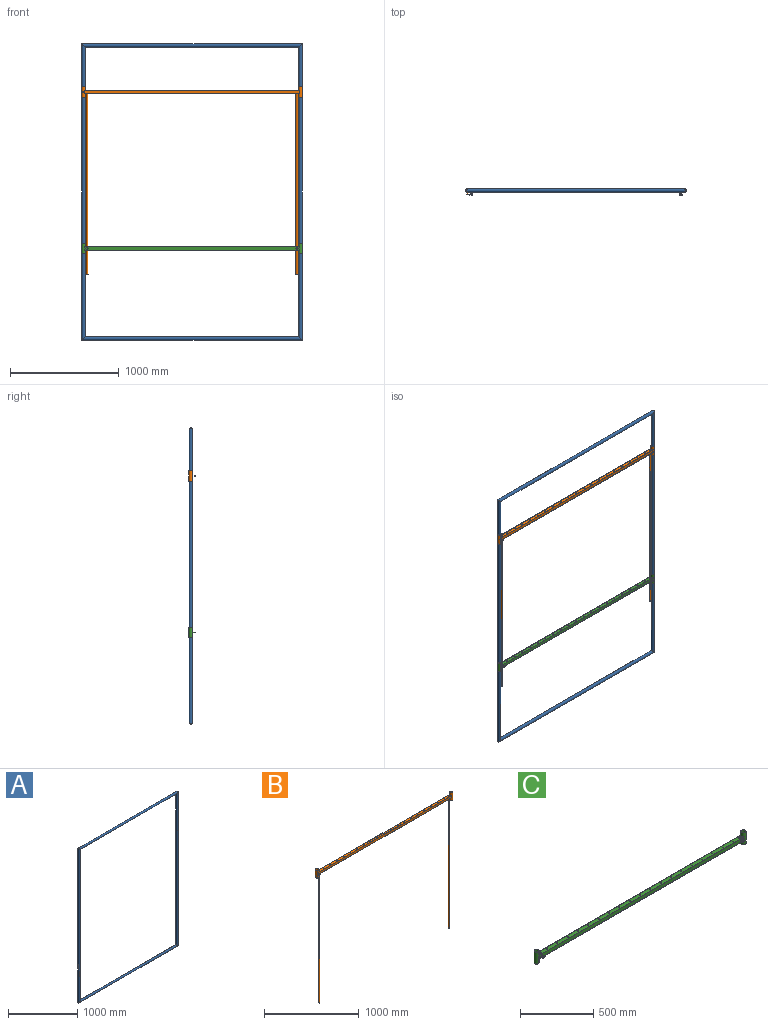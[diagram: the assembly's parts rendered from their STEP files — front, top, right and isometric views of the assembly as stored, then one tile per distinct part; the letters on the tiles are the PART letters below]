
ASSEMBLY  parts=3 mates=2
PART A: 8 faces, bbox 2030x30x2730 mm
  f0: cylinder r=15mm len=2030.02mm, axis (-1,0,0), area 188495.6mm2, adj f1,f3
  f1: cylinder r=15mm len=2730.02mm, axis (0,0,-1), area 254469mm2, adj f0,f2
  f2: cylinder r=15mm len=2030.02mm, axis (1,0,0), area 188495.6mm2, adj f1,f3
  f3: cylinder r=15mm len=2730.02mm, axis (0,0,1), area 254469mm2, adj f0,f2
  f4: cylinder r=13.5mm len=2027.01mm, axis (-1,0,0), area 169646mm2, adj f5,f7
  f5: cylinder r=13.5mm len=2727.01mm, axis (0,0,-1), area 229022.1mm2, adj f4,f6
  f6: cylinder r=13.5mm len=2027.01mm, axis (1,0,0), area 169646mm2, adj f5,f7
  f7: cylinder r=13.5mm len=2727.01mm, axis (0,0,1), area 229022.1mm2, adj f4,f6
PART B: 113 faces, bbox 2035x57.1x1735 mm
  f0: plane 5.12x1.44mm, normal (0,-1,0), area 5.2mm2, adj f96,f100
  f1: plane 9.2x0.1mm, normal (0,-1,0), area 0.9mm2, adj f2,f61,f67,f85
  f2: cylinder r=16mm len=100mm, axis (0,0,1), area 3788.6mm2, adj f1,f4,f49,f50,f59,f60,f61,f62
  f3: cylinder r=17.5mm len=100mm, axis (0,0,1), area 9735.8mm2, adj f49,f50,f51,f52,f53,f54,f87,f88
  f4: cylinder r=16mm len=100mm, axis (0,0,1), area 4969.3mm2, adj f2,f49,f50,f79,f80,f81,f82,f83
  f5: cylinder r=17.5mm len=27mm, axis (0,0,1), area 832.6mm2, adj f6,f7,f8,f9
  f6: plane 1977.73x27mm, normal (0,0,1), area 51802.5mm2, adj f5,f7,f9,f10,f30,f31,f32,f33
  f7: plane 1977.73x27mm, normal (0,-1,0), area 53398.7mm2, adj f5,f6,f8,f10
  f8: plane 1977.73x27mm, normal (0,0,-1), area 51802.5mm2, adj f5,f7,f9,f10,f11,f12,f13,f14
  f9: plane 1977.73x27mm, normal (0,1,0), area 53398.7mm2, adj f5,f6,f8,f10
  f10: cylinder r=17.5mm len=27mm, axis (0,0,1), area 832.6mm2, adj f6,f7,f8,f9
  f11: cylinder r=4mm len=8mm, axis (0,0,1), area 37.7mm2, adj f8,f52
  f12: cylinder r=4mm len=8mm, axis (0,0,1), area 37.7mm2, adj f8,f52
  f13: cylinder r=4mm len=8mm, axis (0,0,1), area 37.7mm2, adj f8,f52
  f14: cylinder r=4mm len=8mm, axis (0,0,1), area 37.7mm2, adj f8,f52
  f15: cylinder r=4mm len=8mm, axis (0,0,1), area 37.7mm2, adj f8,f52
  f16: cylinder r=4mm len=8mm, axis (0,0,1), area 37.7mm2, adj f8,f52
  f17: cylinder r=4mm len=8mm, axis (0,0,1), area 37.7mm2, adj f8,f52
  f18: cylinder r=4mm len=8mm, axis (0,0,1), area 37.7mm2, adj f8,f52
  f19: cylinder r=4mm len=8mm, axis (0,0,1), area 37.7mm2, adj f8,f52
  f20: cylinder r=4mm len=8mm, axis (0,0,1), area 37.7mm2, adj f8,f52
  f21: cylinder r=4mm len=8mm, axis (0,0,1), area 37.7mm2, adj f8,f52
  f22: cylinder r=4mm len=8mm, axis (0,0,1), area 37.7mm2, adj f8,f52
  f23: cylinder r=4mm len=8mm, axis (0,0,1), area 37.7mm2, adj f8,f52
  f24: cylinder r=4mm len=8mm, axis (0,0,1), area 37.7mm2, adj f8,f52
  f25: cylinder r=4mm len=8mm, axis (0,0,1), area 37.7mm2, adj f8,f52
  f26: cylinder r=4mm len=8mm, axis (0,0,1), area 37.7mm2, adj f8,f52
  f27: cylinder r=4mm len=8mm, axis (0,0,1), area 37.7mm2, adj f8,f52
  f28: cylinder r=4mm len=8mm, axis (0,0,1), area 37.7mm2, adj f8,f52
  f29: cylinder r=4mm len=8mm, axis (0,0,1), area 37.7mm2, adj f8,f52
  f30: cylinder r=4mm len=8mm, axis (0,0,1), area 37.7mm2, adj f6,f54
  f31: cylinder r=4mm len=8mm, axis (0,0,1), area 37.7mm2, adj f6,f54
  f32: cylinder r=4mm len=8mm, axis (0,0,1), area 37.7mm2, adj f6,f54
  f33: cylinder r=4mm len=8mm, axis (0,0,1), area 37.7mm2, adj f6,f54
  f34: cylinder r=4mm len=8mm, axis (0,0,1), area 37.7mm2, adj f6,f54
  f35: cylinder r=4mm len=8mm, axis (0,0,1), area 37.7mm2, adj f6,f54
  f36: cylinder r=4mm len=8mm, axis (0,0,1), area 37.7mm2, adj f6,f54
  f37: cylinder r=4mm len=8mm, axis (0,0,1), area 37.7mm2, adj f6,f54
  f38: cylinder r=4mm len=8mm, axis (0,0,1), area 37.7mm2, adj f6,f54
  f39: cylinder r=4mm len=8mm, axis (0,0,1), area 37.7mm2, adj f6,f54
  f40: cylinder r=4mm len=8mm, axis (0,0,1), area 37.7mm2, adj f6,f54
  f41: cylinder r=4mm len=8mm, axis (0,0,1), area 37.7mm2, adj f6,f54
  f42: cylinder r=4mm len=8mm, axis (0,0,1), area 37.7mm2, adj f6,f54
  f43: cylinder r=4mm len=8mm, axis (0,0,1), area 37.7mm2, adj f6,f54
  f44: cylinder r=4mm len=8mm, axis (0,0,1), area 37.7mm2, adj f6,f54
  f45: cylinder r=4mm len=8mm, axis (0,0,1), area 37.7mm2, adj f6,f54
  f46: cylinder r=4mm len=8mm, axis (0,0,1), area 37.7mm2, adj f6,f54
  f47: cylinder r=4mm len=8mm, axis (0,0,1), area 37.7mm2, adj f6,f54
  f48: cylinder r=4mm len=8mm, axis (0,0,1), area 37.7mm2, adj f6,f54
  f49: plane 35x35mm, normal (0,0,-1), area 154.7mm2, adj f2,f3,f4
  f50: plane 35x35mm, normal (0,0,1), area 154.7mm2, adj f2,f3,f4
  f51: plane 1981.97x30mm, normal (0,1,0), area 59459.2mm2, adj f3,f52,f54,f58
  f52: plane 1981.97x30mm, normal (0,0,1), area 58143.9mm2, adj f3,f11,f12,f13,f14,f15,f16,f17
  f53: plane 1981.97x30mm, normal (0,-1,0), area 59459.2mm2, adj f3,f52,f54,f58
  f54: plane 1981.97x30mm, normal (0,0,-1), area 57741.7mm2, adj f3,f30,f31,f32,f33,f34,f35,f36
  f55: plane 35x35mm, normal (0,0,1), area 157.9mm2, adj f57,f58
  f56: plane 35x35mm, normal (0,0,-1), area 157.9mm2, adj f57,f58
  f57: cylinder r=16mm len=100mm, axis (0,0,1), area 10053.1mm2, adj f55,f56
  f58: cylinder r=17.5mm len=100mm, axis (0,0,1), area 9914.4mm2, adj f51,f52,f53,f54,f55,f56
  f59: plane 30x10.53mm, normal (0,0,-1), area 3mm2, adj f2,f60,f62,f67
  f60: plane 8.62x0.1mm, normal (0,-1,0), area 0.9mm2, adj f2,f59,f67,f86
  f61: plane 30x10.53mm, normal (0,0,1), area 3mm2, adj f1,f2,f62,f67
  f62: plane 30x0.1mm, normal (0,1,0), area 3mm2, adj f2,f59,f61,f67
  f63: plane 27x0.1mm, normal (0,1,0), area 2.7mm2, adj f64,f66,f67,f68
  f64: plane 27x7.51mm, normal (0,0,-1), area 2.7mm2, adj f63,f65,f67,f68
  f65: plane 27x0.1mm, normal (0,-1,0), area 2.7mm2, adj f64,f66,f67,f68
  f66: plane 27x7.51mm, normal (0,0,1), area 2.7mm2, adj f63,f65,f67,f68
  f67: cylinder r=16mm len=30mm, axis (0,0,1), area 299.1mm2, adj f1,f59,f60,f61,f62,f63,f64,f65
  f68: cylinder r=16mm len=27mm, axis (0,0,1), area 867.7mm2, adj f63,f64,f65,f66
  f69: cylinder r=6.5mm len=1670mm, axis (0,0,-1), area 68204mm2, adj f70,f72
  f70: plane 16x16mm, normal (0,0,-1), area 68.3mm2, adj f69,f71
  f71: cylinder r=8mm len=1670mm, axis (0,0,-1), area 83943.4mm2, adj f54,f70
  f72: plane 13x13mm, normal (0,0,-1), area 132.7mm2, adj f69
  f73: cylinder r=8mm len=27mm, axis (0,0,-1), area 1357.2mm2, adj f6,f8
  f74: cylinder r=6.5mm len=1670mm, axis (0,0,-1), area 68204mm2, adj f75,f77
  f75: plane 16x16mm, normal (0,0,-1), area 68.3mm2, adj f74,f76
  f76: cylinder r=8mm len=1670mm, axis (0,0,-1), area 83943.4mm2, adj f54,f75
  f77: plane 13x13mm, normal (0,0,-1), area 132.7mm2, adj f74
  f78: cylinder r=8mm len=27mm, axis (0,0,-1), area 1357.2mm2, adj f6,f8
  f79: plane 15.28x11.14mm, normal (0,1,0), area 144.5mm2, adj f4,f67,f80,f81,f82,f83,f84,f85
  f80: plane 3.83x2.73mm, normal (-0.81,0,0.58), area 2mm2, adj f4,f79,f81
  f81: plane 5.92x1mm, normal (-0.17,0,0.99), area 5.5mm2, adj f2,f4,f79,f80,f85
  f82: plane 5.93x1.01mm, normal (0.17,0,-0.99), area 4.3mm2, adj f2,f4,f79,f83,f86
  f83: plane 4.89x3.48mm, normal (-0.58,0,-0.81), area 4mm2, adj f4,f79,f82,f84
  f84: plane 1.46x0.25mm, normal (-0.99,0,-0.17), area 0.1mm2, adj f4,f79,f83
  f85: plane 2.59x1.84mm, normal (0.58,0,0.81), area 1.3mm2, adj f1,f2,f79,f81
  f86: plane 0.26x0.18mm, normal (0.81,0,-0.58), area 0mm2, adj f2,f60,f79,f82
  f87: plane 5.93x4.36mm, normal (0.17,0,-0.99), area 22.5mm2, adj f3,f90,f91,f95
  f88: plane 5.92x3.76mm, normal (-0.17,0,0.99), area 21.5mm2, adj f3,f93,f94,f95
  f89: plane 5.92x4.72mm, normal (-0.99,0,-0.17), area 27.2mm2, adj f3,f90,f94,f95
  f90: plane 4.89x4.36mm, normal (-0.58,0,-0.81), area 22.9mm2, adj f3,f87,f89,f95
  f91: plane 5.91x4.89mm, normal (0.81,0,-0.58), area 30.3mm2, adj f3,f87,f92,f95
  f92: plane 5.92x5.91mm, normal (0.99,0,0.17), area 33.8mm2, adj f3,f91,f93,f95
  f93: plane 5.37x4.89mm, normal (0.58,0,0.81), area 26.6mm2, adj f3,f88,f92,f95
  f94: plane 4.89x4.72mm, normal (-0.81,0,0.58), area 25mm2, adj f3,f88,f89,f95
  f95: plane 15.28x15.28mm, normal (0,-1,0), area 145.5mm2, adj f87,f88,f89,f90,f91,f92,f93,f94
  f96: cylinder r=3mm len=15mm, axis (0,1,0), area 263.8mm2, adj f0,f95,f97,f98,f99,f100,f101
  f97: plane 5.27x1.56mm, normal (0,-1,0), area 5.9mm2, adj f96,f99
  f98: plane 9.96x3mm, normal (0,1,0), area 29mm2, adj f96,f99,f100,f106
  f99: plane 25.28x6.64mm, normal (0,0,1), area 141.2mm2, adj f96,f97,f98,f101,f102,f103,f104,f105
  f100: plane 25.28x6.64mm, normal (0,0,-1), area 141.6mm2, adj f0,f96,f98,f101,f102,f103,f104,f105
  f101: plane 10.19x3mm, normal (0,1,0), area 29.7mm2, adj f96,f99,f100,f102
  f102: plane 3x1.64mm, normal (-1,0,0), area 4.9mm2, adj f99,f100,f101,f103
  f103: cylinder r=5mm len=5mm, axis (0,0,-1), area 23.6mm2, adj f99,f100,f102,f104
  f104: plane 15.28x3mm, normal (0,-1,0), area 45.8mm2, adj f99,f100,f103,f105
  f105: cylinder r=5mm len=5mm, axis (0,0,-1), area 23.6mm2, adj f99,f100,f104,f106
  f106: plane 3x1.64mm, normal (1,0,0), area 4.9mm2, adj f98,f99,f100,f105
  f107: cylinder r=6.5mm len=27mm, axis (0,0,-1), area 1102.7mm2, adj f108,f109
  f108: plane 13x13mm, normal (0,0,-1), area 132.7mm2, adj f107
  f109: plane 13x13mm, normal (0,0,1), area 132.7mm2, adj f107
  f110: cylinder r=6.5mm len=27mm, axis (0,0,-1), area 1102.7mm2, adj f111,f112
  f111: plane 13x13mm, normal (0,0,-1), area 132.7mm2, adj f110
  f112: plane 13x13mm, normal (0,0,1), area 132.7mm2, adj f110
PART C: 107 faces, bbox 2035x58.9x100 mm
  f0: plane 5.13x1.44mm, normal (0,-1,0), area 5.2mm2, adj f89,f106
  f1: plane 5.13x1.44mm, normal (0,-1,0), area 5.2mm2, adj f87,f93
  f2: plane 1981.97x30mm, normal (0,-1,0), area 59126.6mm2, adj f5,f6,f50,f58,f73,f74,f75,f76
  f3: plane 1977.73x27mm, normal (0,0,1), area 51576.3mm2, adj f7,f8,f9,f10,f30,f31,f32,f33
  f4: plane 1977.73x27mm, normal (0,0,-1), area 51576.3mm2, adj f7,f8,f9,f10,f11,f12,f13,f14
  f5: plane 1981.97x30mm, normal (0,0,1), area 57515.5mm2, adj f2,f11,f12,f13,f14,f15,f16,f17
  f6: plane 1981.97x30mm, normal (0,0,-1), area 57515.5mm2, adj f2,f30,f31,f32,f33,f34,f35,f36
  f7: cylinder r=17.5mm len=27mm, axis (0,0,1), area 832.6mm2, adj f3,f4,f8,f9
  f8: plane 1977.73x27mm, normal (0,-1,0), area 53398.7mm2, adj f3,f4,f7,f10
  f9: plane 1977.73x27mm, normal (0,1,0), area 53398.7mm2, adj f3,f4,f7,f10
  f10: cylinder r=17.5mm len=27mm, axis (0,0,1), area 832.6mm2, adj f3,f4,f8,f9
  f11: cylinder r=4mm len=8mm, axis (0,0,1), area 37.7mm2, adj f4,f5
  f12: cylinder r=4mm len=8mm, axis (0,0,1), area 37.7mm2, adj f4,f5
  f13: cylinder r=4mm len=8mm, axis (0,0,1), area 37.7mm2, adj f4,f5
  f14: cylinder r=4mm len=8mm, axis (0,0,1), area 37.7mm2, adj f4,f5
  f15: cylinder r=4mm len=8mm, axis (0,0,1), area 37.7mm2, adj f4,f5
  f16: cylinder r=4mm len=8mm, axis (0,0,1), area 37.7mm2, adj f4,f5
  f17: cylinder r=4mm len=8mm, axis (0,0,1), area 37.7mm2, adj f4,f5
  f18: cylinder r=4mm len=8mm, axis (0,0,1), area 37.7mm2, adj f4,f5
  f19: cylinder r=4mm len=8mm, axis (0,0,1), area 37.7mm2, adj f4,f5
  f20: cylinder r=4mm len=8mm, axis (0,0,1), area 37.7mm2, adj f4,f5
  f21: cylinder r=4mm len=8mm, axis (0,0,1), area 37.7mm2, adj f4,f5
  f22: cylinder r=4mm len=8mm, axis (0,0,1), area 37.7mm2, adj f4,f5
  f23: cylinder r=4mm len=8mm, axis (0,0,1), area 37.7mm2, adj f4,f5
  f24: cylinder r=4mm len=8mm, axis (0,0,1), area 37.7mm2, adj f4,f5
  f25: cylinder r=4mm len=8mm, axis (0,0,1), area 37.7mm2, adj f4,f5
  f26: cylinder r=4mm len=8mm, axis (0,0,1), area 37.7mm2, adj f4,f5
  f27: cylinder r=4mm len=8mm, axis (0,0,1), area 37.7mm2, adj f4,f5
  f28: cylinder r=4mm len=8mm, axis (0,0,1), area 37.7mm2, adj f4,f5
  f29: cylinder r=4mm len=8mm, axis (0,0,1), area 37.7mm2, adj f4,f5
  f30: cylinder r=4mm len=8mm, axis (0,0,1), area 37.7mm2, adj f3,f6
  f31: cylinder r=4mm len=8mm, axis (0,0,1), area 37.7mm2, adj f3,f6
  f32: cylinder r=4mm len=8mm, axis (0,0,1), area 37.7mm2, adj f3,f6
  f33: cylinder r=4mm len=8mm, axis (0,0,1), area 37.7mm2, adj f3,f6
  f34: cylinder r=4mm len=8mm, axis (0,0,1), area 37.7mm2, adj f3,f6
  f35: cylinder r=4mm len=8mm, axis (0,0,1), area 37.7mm2, adj f3,f6
  f36: cylinder r=4mm len=8mm, axis (0,0,1), area 37.7mm2, adj f3,f6
  f37: cylinder r=4mm len=8mm, axis (0,0,1), area 37.7mm2, adj f3,f6
  f38: cylinder r=4mm len=8mm, axis (0,0,1), area 37.7mm2, adj f3,f6
  f39: cylinder r=4mm len=8mm, axis (0,0,1), area 37.7mm2, adj f3,f6
  f40: cylinder r=4mm len=8mm, axis (0,0,1), area 37.7mm2, adj f3,f6
  f41: cylinder r=4mm len=8mm, axis (0,0,1), area 37.7mm2, adj f3,f6
  f42: cylinder r=4mm len=8mm, axis (0,0,1), area 37.7mm2, adj f3,f6
  f43: cylinder r=4mm len=8mm, axis (0,0,1), area 37.7mm2, adj f3,f6
  f44: cylinder r=4mm len=8mm, axis (0,0,1), area 37.7mm2, adj f3,f6
  f45: cylinder r=4mm len=8mm, axis (0,0,1), area 37.7mm2, adj f3,f6
  f46: cylinder r=4mm len=8mm, axis (0,0,1), area 37.7mm2, adj f3,f6
  f47: cylinder r=4mm len=8mm, axis (0,0,1), area 37.7mm2, adj f3,f6
  f48: cylinder r=4mm len=8mm, axis (0,0,1), area 37.7mm2, adj f3,f6
  f49: cylinder r=16mm len=100mm, axis (0,0,1), area 3869.8mm2, adj f51,f52,f53,f59,f60,f61,f62
  f50: cylinder r=17.5mm len=100mm, axis (0,0,1), area 9914.4mm2, adj f2,f5,f6,f51,f52,f54
  f51: plane 35x35mm, normal (0,0,-1), area 154.7mm2, adj f49,f50,f53
  f52: plane 35x35mm, normal (0,0,1), area 154.7mm2, adj f49,f50,f53
  f53: cylinder r=16mm len=100mm, axis (0,0,1), area 5036.6mm2, adj f49,f51,f52
  f54: plane 1981.97x30mm, normal (0,1,0), area 59459.2mm2, adj f5,f6,f50,f58
  f55: plane 35x35mm, normal (0,0,1), area 157.9mm2, adj f57,f58
  f56: plane 35x35mm, normal (0,0,-1), area 157.9mm2, adj f57,f58
  f57: cylinder r=16mm len=100mm, axis (0,0,1), area 10053.1mm2, adj f55,f56
  f58: cylinder r=17.5mm len=100mm, axis (0,0,1), area 9914.4mm2, adj f2,f5,f6,f54,f55,f56
  f59: plane 30x10.53mm, normal (0,0,-1), area 3mm2, adj f49,f60,f62,f67
  f60: plane 30x0.1mm, normal (0,-1,0), area 3mm2, adj f49,f59,f61,f67
  f61: plane 30x10.53mm, normal (0,0,1), area 3mm2, adj f49,f60,f62,f67
  f62: plane 30x0.1mm, normal (0,1,0), area 3mm2, adj f49,f59,f61,f67
  f63: plane 27x0.1mm, normal (0,1,0), area 2.7mm2, adj f64,f66,f67,f68
  f64: plane 27x7.51mm, normal (0,0,-1), area 2.7mm2, adj f63,f65,f67,f68
  f65: plane 27x0.1mm, normal (0,-1,0), area 2.7mm2, adj f64,f66,f67,f68
  f66: plane 27x7.51mm, normal (0,0,1), area 2.7mm2, adj f63,f65,f67,f68
  f67: cylinder r=16mm len=30mm, axis (0,0,1), area 299.1mm2, adj f59,f60,f61,f62,f63,f64,f65,f66
  f68: cylinder r=16mm len=27mm, axis (0,0,1), area 867.7mm2, adj f63,f64,f65,f66
  f69: cylinder r=10mm len=20mm, axis (0,0,1), area 94.2mm2, adj f3,f6
  f70: cylinder r=10mm len=20mm, axis (0,0,1), area 94.2mm2, adj f3,f6
  f71: cylinder r=10mm len=20mm, axis (0,0,1), area 94.2mm2, adj f4,f5
  f72: cylinder r=10mm len=20mm, axis (0,0,1), area 94.2mm2, adj f4,f5
  f73: plane 7.8x6mm, normal (-0.98,0,0.22), area 48mm2, adj f2,f74,f78,f79
  f74: plane 6x5.87mm, normal (-0.68,0,-0.73), area 48mm2, adj f2,f73,f75,f79
  f75: plane 7.64x6mm, normal (0.3,0,-0.96), area 48mm2, adj f2,f74,f76,f79
  f76: plane 7.8x6mm, normal (0.98,0,-0.22), area 48mm2, adj f2,f75,f77,f79
  f77: plane 6x5.87mm, normal (0.68,0,0.73), area 48mm2, adj f2,f76,f78,f79
  f78: plane 7.64x6mm, normal (-0.3,0,0.96), area 48mm2, adj f2,f73,f77,f79
  f79: plane 15.6x15.28mm, normal (0,-1,0), area 138mm2, adj f73,f74,f75,f76,f77,f78,f87
  f80: plane 7.8x6mm, normal (-0.98,0,-0.22), area 48mm2, adj f2,f81,f85,f86
  f81: plane 7.64x6mm, normal (-0.3,0,-0.96), area 48mm2, adj f2,f80,f82,f86
  f82: plane 6x5.87mm, normal (0.68,0,-0.73), area 48mm2, adj f2,f81,f83,f86
  f83: plane 7.8x6mm, normal (0.98,0,0.22), area 48mm2, adj f2,f82,f84,f86
  f84: plane 7.64x6mm, normal (0.3,0,0.96), area 48mm2, adj f2,f83,f85,f86
  f85: plane 6x5.87mm, normal (-0.68,0,0.73), area 48mm2, adj f2,f80,f84,f86
  f86: plane 15.6x15.28mm, normal (0,-1,0), area 138mm2, adj f80,f81,f82,f83,f84,f85,f89
  f87: cylinder r=3mm len=15mm, axis (0,1,0), area 274.3mm2, adj f1,f79,f88,f91,f92,f93,f94
  f88: plane 5.26x1.56mm, normal (0,-1,0), area 5.8mm2, adj f87,f92
  f89: cylinder r=3mm len=15mm, axis (0,1,0), area 274.3mm2, adj f0,f86,f90,f100,f103,f105,f106
  f90: plane 5.26x1.56mm, normal (0,-1,0), area 5.8mm2, adj f89,f105
  f91: plane 11.79x3mm, normal (0,1,0), area 34.4mm2, adj f87,f92,f93,f99
  f92: plane 30.9x6.72mm, normal (0,0,1), area 189.8mm2, adj f87,f88,f91,f94,f95,f96,f97,f98
  f93: plane 30.9x6.72mm, normal (0,0,-1), area 190mm2, adj f1,f87,f91,f94,f95,f96,f97,f98
  f94: plane 13.99x3mm, normal (0,1,0), area 41mm2, adj f87,f92,f93,f95
  f95: plane 3x1.72mm, normal (-1,0,0), area 5.2mm2, adj f92,f93,f94,f96
  f96: cylinder r=5mm len=5mm, axis (0,0,-1), area 23.6mm2, adj f92,f93,f95,f97
  f97: plane 20.9x3mm, normal (0,-1,0), area 62.7mm2, adj f92,f93,f96,f98
  f98: cylinder r=5mm len=5mm, axis (0,0,-1), area 23.6mm2, adj f92,f93,f97,f99
  f99: plane 3x1.72mm, normal (1,0,0), area 5.2mm2, adj f91,f92,f93,f98
  f100: plane 11.79x3mm, normal (0,1,0), area 34.4mm2, adj f89,f104,f105,f106
  f101: plane 30.9x3mm, normal (0,-1,0), area 92.7mm2, adj f102,f104,f105,f106
  f102: plane 6.72x3mm, normal (1,0,0), area 20.2mm2, adj f101,f103,f105,f106
  f103: plane 13.99x3mm, normal (0,1,0), area 41mm2, adj f89,f102,f105,f106
  f104: plane 6.72x3mm, normal (-1,0,0), area 20.2mm2, adj f100,f101,f105,f106
  f105: plane 30.9x6.72mm, normal (0,0,1), area 200.6mm2, adj f89,f90,f100,f101,f102,f103,f104
  f106: plane 30.9x6.72mm, normal (0,0,-1), area 200.7mm2, adj f0,f89,f100,f101,f102,f103,f104
PLACE A at identity fixed
PLACE B t=(0,0,-818.57)mm
PLACE C t=(0,0,-2070.69)mm
MATE slider A.f3 <-> B.f2  axis (0,0,1) through (-1000,0,0)mm
MATE slider A.f3 <-> C.f10  axis (0,0,1) through (-1000,0,0)mm
